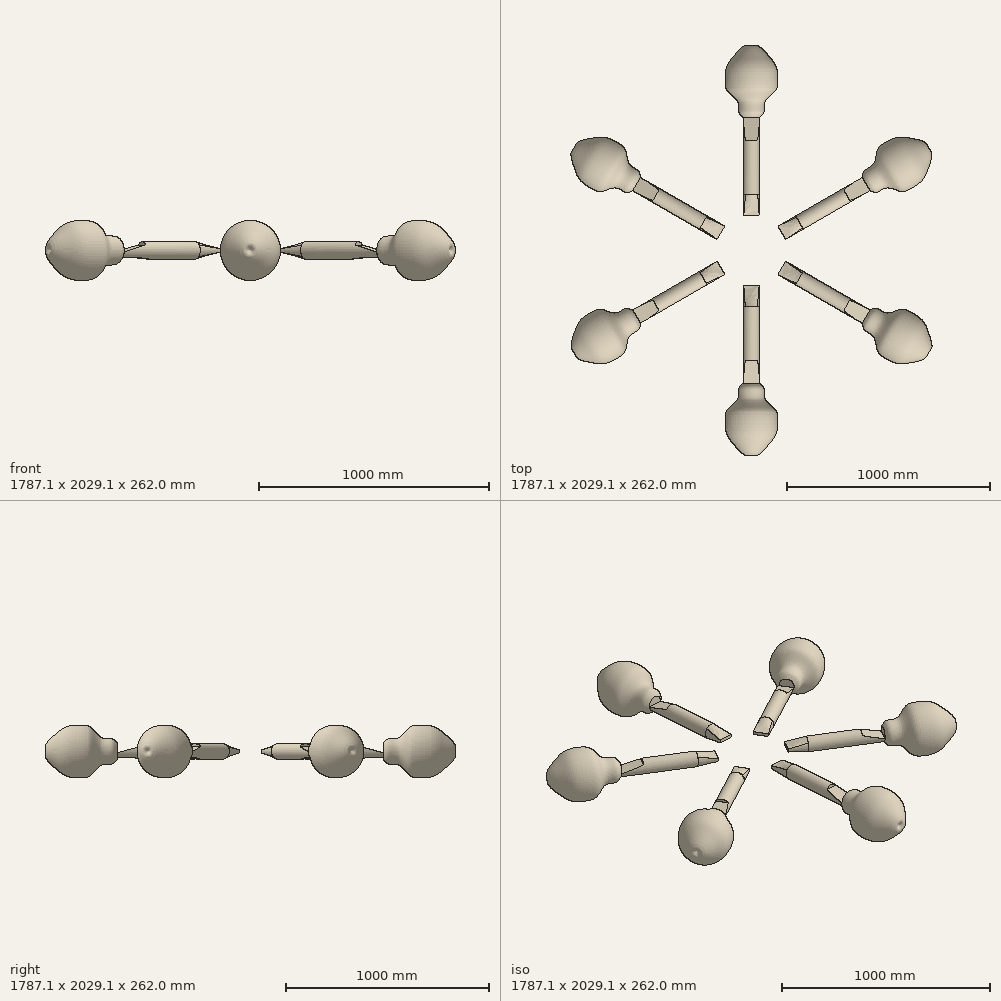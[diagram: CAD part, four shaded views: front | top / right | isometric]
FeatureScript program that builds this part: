
annotation { "Feature Type Name" : "Feature", "Feature Type Description" : "" }
export const myFeature = defineFeature(function(context is Context, id is Id, definition is map)
    precondition{}
    {
        {
            var Q0;
            Q0=qCreatedBy(makeId("Front.planeOp"),FACE);
            cPlane(context, id + "F0", {"entities" : qUnion([Q0]), "cplaneType" : CPlaneType.OFFSET, "offset" : 101.6 * mm, "width" : 152.4 * mm, "height" : 152.4 * mm});
        }
        {
            var Q0;
            Q0=qCreatedBy(makeId("Front.planeOp"),FACE);
            var sketch = newSketch(context, id + "F1", { "sketchPlane" : qUnion([Q0])});
            skArc(sketch, "E0", {"start": v(-29.14, 24.54) * mm, "mid": v(-38.06, -1.69) * mm, "end": v(-26.86, -27.03) * mm});
            skArc(sketch, "E1", {"start": v(30.89, 22.3) * mm, "mid": v(1.42, 38.07) * mm, "end": v(-29.14, 24.54) * mm});
            skArc(sketch, "E2", {"start": v(27.96, -25.88) * mm, "mid": v(38.03, -2.31) * mm, "end": v(30.89, 22.3) * mm});
            skArc(sketch, "E3", {"start": v(-26.86, -27.03) * mm, "mid": v(0.8, -38.1) * mm, "end": v(27.96, -25.88) * mm});
            skSolve(sketch);
        }
        {
            var Q0;
            Q0=qCreatedBy(id+"F0.planeOp",FACE);
            var sketch = newSketch(context, id + "F2", { "sketchPlane" : qUnion([Q0])});
            skLineSegment(sketch, "E4.bottom", {"start": v(38.1, -7.62) * mm, "end": v(-38.1, -7.62) * mm});
            skLineSegment(sketch, "E4.top", {"start": v(38.1, 7.62) * mm, "end": v(-38.1, 7.62) * mm});
            skLineSegment(sketch, "E4.left", {"start": v(38.1, -7.62) * mm, "end": v(38.1, 7.62) * mm});
            skLineSegment(sketch, "E4.right", {"start": v(-38.1, -7.62) * mm, "end": v(-38.1, 7.62) * mm});
            skPoint(sketch, "E4.middle", {"position": v(0, 0) * mm});
            skSolve(sketch);
        }
        {
            var Q0;
            Q0=makeQuery(id+"F1.imprint","IMPRINT",FACE,{"disambiguationData":[TD([[makeQuery(id+"F1.imprint","IMPRINT",EDGE,{"derivedFrom":sQuery(id+"F1.wireOp",EDGE,"E0")}),1.0]])]});
            var Q1;
            Q1=makeQuery(id+"F2.imprint","IMPRINT",FACE,{"disambiguationData":[TD([[makeQuery(id+"F2.imprint","IMPRINT",EDGE,{"derivedFrom":sQuery(id+"F2.wireOp",EDGE,"E4.bottom")}),-1.0]])]});
            loft(context, id + "F3", {"sheetProfilesArray" : [{ "sheetProfileEntities" : qUnion([Q0]) }, { "sheetProfileEntities" : qUnion([Q1]) }]});
        }
        {
            var Q0;
            Q0=qCreatedBy(makeId("Front.planeOp"),FACE);
            cPlane(context, id + "F4", {"entities" : qUnion([Q0]), "cplaneType" : CPlaneType.OFFSET, "offset" : 0 * mm, "oppositeDirection" : true, "width" : 152.4 * mm, "height" : 152.4 * mm});
        }
        {
            var Q0;
            Q0=qCreatedBy(id+"F4.planeOp",FACE);
            var sketch = newSketch(context, id + "F5", { "sketchPlane" : qUnion([Q0])});
            skCircle(sketch, "E5", {"center": v(0, 0) * mm, "radius": 38.09 * mm});
            skSolve(sketch);
        }
        {
            var Q0;
            Q0 = qSketchRegion(id + "F5", true);
            extrude(context, id + "F6", {"entities" : qUnion([Q0]), "operationType" : NewBodyOperationType.ADD, "oppositeDirection" : true, "depth" : 381 * mm});
        }
        {
            var Q0;
            Q0=qCreatedBy(makeId("Right.planeOp"),FACE);
            var sketch = newSketch(context, id + "F7", { "sketchPlane" : qUnion([Q0])});
            skLineSegment(sketch, "E6", {"start": v(269.92, 75.71) * mm, "end": v(269.92, 55.1) * mm});
            skLineSegment(sketch, "E7", {"start": v(269.92, 55.1) * mm, "end": v(269.92, 23.57) * mm});
            skLineSegment(sketch, "E8", {"start": v(269.92, 23.57) * mm, "end": v(401.31, -10.9) * mm});
            skLineSegment(sketch, "E9", {"start": v(401.31, -10.9) * mm, "end": v(401.31, -27.4) * mm});
            skLineSegment(sketch, "E10", {"start": v(401.31, -27.4) * mm, "end": v(244.58, -34.47) * mm});
            skLineSegment(sketch, "E11", {"start": v(244.58, -34.47) * mm, "end": v(233.1, -48.61) * mm});
            skLineSegment(sketch, "E12", {"start": v(233.1, -48.61) * mm, "end": v(233.1, -63.34) * mm});
            skLineSegment(sketch, "E13", {"start": v(233.1, -63.34) * mm, "end": v(428.71, -49.79) * mm});
            skLineSegment(sketch, "E14", {"start": v(428.71, -49.79) * mm, "end": v(425.47, 74.54) * mm});
            skLineSegment(sketch, "E15", {"start": v(425.47, 74.54) * mm, "end": v(269.92, 75.71) * mm});
            skSolve(sketch);
        }
        {
            var Q0;
            Q0=makeQuery(id+"F7.imprint","IMPRINT",FACE,{"disambiguationData":[TD([[makeQuery(id+"F7.imprint","IMPRINT",EDGE,{"derivedFrom":sQuery(id+"F7.wireOp",EDGE,"E6")}),1.0]])]});
            extrude(context, id + "F8", {"entities" : qUnion([Q0]), "operationType" : NewBodyOperationType.REMOVE, "endBound" : BoundingType.SYMMETRIC, "depth" : 152.4 * mm});
        }
        {
            var Q0;
            Q0=qCreatedBy(makeId("Top.planeOp"),FACE);
            var sketch = newSketch(context, id + "F9", { "sketchPlane" : qUnion([Q0])});
            skLineSegment(sketch, "E16", {"start": v(0, 380.9) * mm, "end": v(0, 579.99) * mm, "construction": true});
            skFitSpline(sketch, "E17", {"points": [v(-36.55, 380.9) * mm, v(-61.37, 405.72) * mm, v(-67.57, 460.43) * mm, v(-113.25, 507.24) * mm, v(-129.6, 546.15) * mm, v(-123.8, 628.88) * mm, v(-87.36, 685.64) * mm, v(-26.42, 739.41) * mm, v(0, 722.68) * mm], "startDerivative": vector(-319.4, 199.99) * mm, "endDerivative": vector(252, -290.8) * mm});
            skLineSegment(sketch, "E18", {"start": v(0, 722.68) * mm, "end": v(0, 380.9) * mm});
            skLineSegment(sketch, "E19", {"start": v(-36.55, 380.9) * mm, "end": v(0, 380.9) * mm});
            skSolve(sketch);
        }
        {
            var Q0;
            Q0=makeQuery(id+"F9.imprint","IMPRINT",FACE,{"disambiguationData":[TD([[makeQuery(id+"F9.imprint","IMPRINT",EDGE,{"derivedFrom":sQuery(id+"F9.wireOp",EDGE,"E17")}),-1.0]])]});
            var Q1;
            Q1=sQuery(id+"F9.wireOp",EDGE,"E18");
            revolve(context, id + "F10", {"operationType" : NewBodyOperationType.ADD, "entities" : qUnion([Q0]), "axis" : qUnion([Q1]), "revolveType" : RevolveType.FULL});
        }
        {
            var Q0;
            Q0=qCreatedBy(makeId("Right.planeOp"),FACE);
            var sketch = newSketch(context, id + "F11", { "sketchPlane" : qUnion([Q0])});
            skLineSegment(sketch, "E20", {"start": v(-274.99, 79.62) * mm, "end": v(-274.99, -165) * mm, "construction": true});
            skSolve(sketch);
        }
        {
            var Q0;
            Q0=makeQuery(id+"F3.opLoft","SWEPT_BODY",BODY,{"disambiguationData":[OSD([makeQuery(id+"F1.imprint","IMPRINT",FACE,{"disambiguationData":[TD([[makeQuery(id+"F1.imprint","IMPRINT",EDGE,{"derivedFrom":sQuery(id+"F1.wireOp",EDGE,"E0")}),1.0]])]}),makeQuery(id+"F2.imprint","IMPRINT",FACE,{"disambiguationData":[TD([[makeQuery(id+"F2.imprint","IMPRINT",EDGE,{"derivedFrom":sQuery(id+"F2.wireOp",EDGE,"E4.bottom")}),-1.0]])]})])]});
            var Q1;
            Q1=sQuery(id+"F11.wireOp",EDGE,"E20");
            circularPattern(context, id + "F12", {"entities" : qUnion([Q0]), "axis" : qUnion([Q1]), "angle" : 360 * degree, "instanceCount" : 6, "oppositeDirection" : true, "equalSpace" : true});
        }
    });
